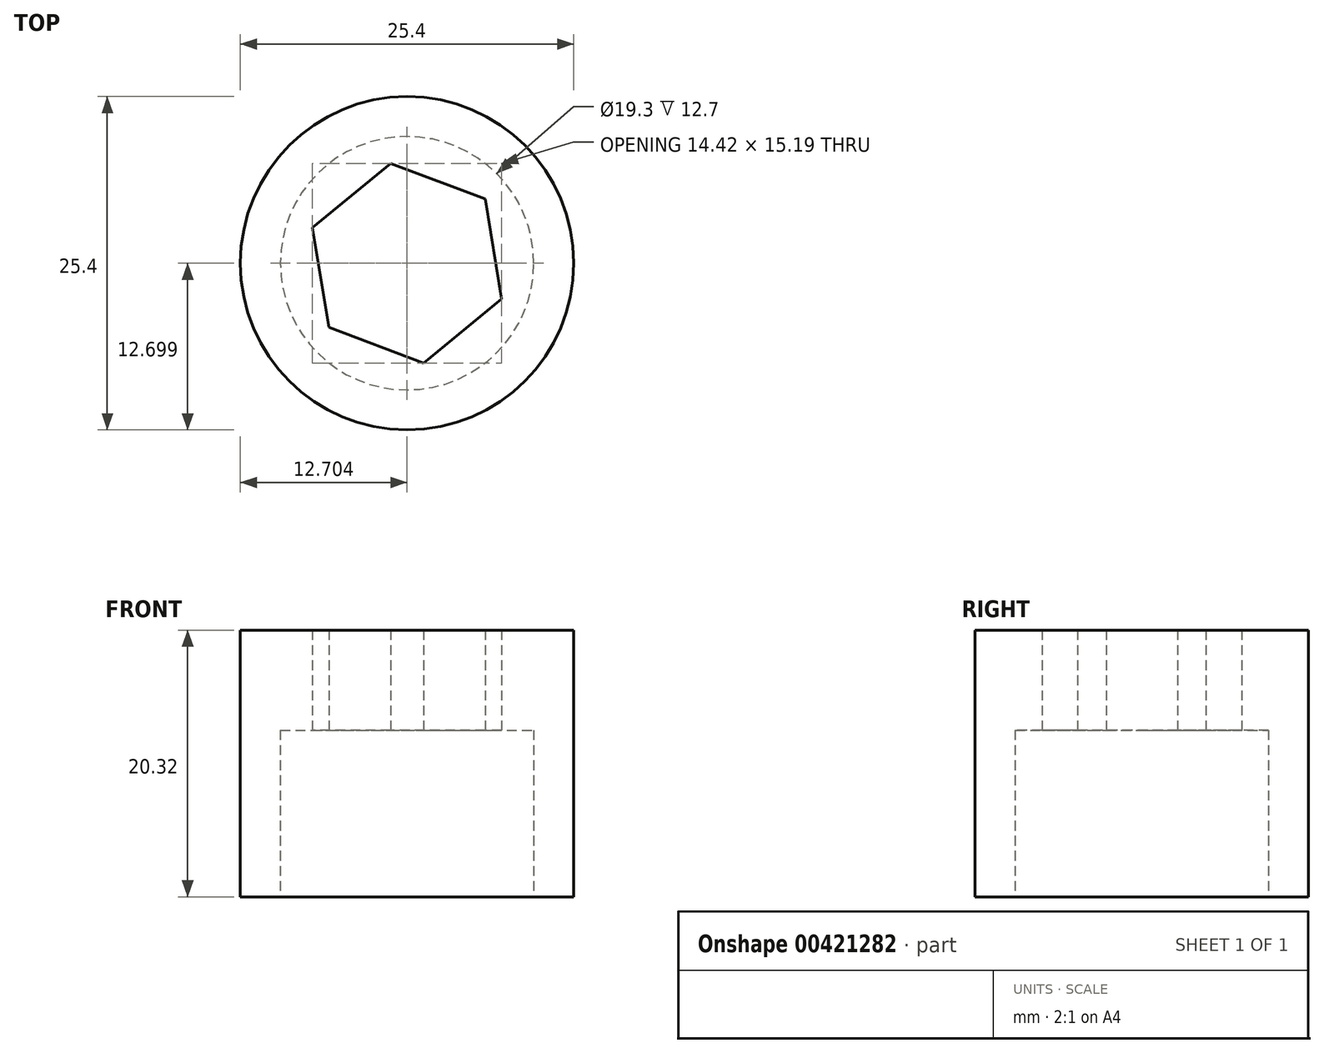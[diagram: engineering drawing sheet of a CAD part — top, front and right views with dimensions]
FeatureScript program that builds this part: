
annotation { "Feature Type Name" : "Feature", "Feature Type Description" : "" }
export const myFeature = defineFeature(function(context is Context, id is Id, definition is map)
    precondition{}
    {
        {
            var Q0;
            Q0=qCreatedBy(makeId("Top.planeOp"),FACE);
            var sketch = newSketch(context, id + "F0", { "sketchPlane" : qUnion([Q0])});
            skCircle(sketch, "E0", {"center": v(-39.24, 31.02) * mm, "radius": 12.7 * mm});
            skCircle(sketch, "E1", {"center": v(-39.24, 31.02) * mm, "radius": 10.16 * mm});
            skCircle(sketch, "E2.cCircle", {"center": v(-39.24, 31.02) * mm, "radius": 7.7 * mm, "construction": true});
            skLineSegment(sketch, "E2.0", {"start": v(-33.29, 35.9) * mm, "end": v(-32.03, 28.31) * mm});
            skLineSegment(sketch, "E2.1", {"start": v(-32.03, 28.31) * mm, "end": v(-37.97, 23.42) * mm});
            skLineSegment(sketch, "E2.2", {"start": v(-37.97, 23.42) * mm, "end": v(-45.18, 26.13) * mm});
            skLineSegment(sketch, "E2.3", {"start": v(-45.18, 26.13) * mm, "end": v(-46.44, 33.72) * mm});
            skLineSegment(sketch, "E2.4", {"start": v(-46.44, 33.72) * mm, "end": v(-40.5, 38.61) * mm});
            skLineSegment(sketch, "E2.5", {"start": v(-40.5, 38.61) * mm, "end": v(-33.29, 35.9) * mm});
            skSolve(sketch);
        }
        {
            var Q0;
            Q0=makeQuery(id+"F0.imprint","IMPRINT",FACE,{"disambiguationData":[TD([[makeQuery(id+"F0.imprint","IMPRINT",EDGE,{"derivedFrom":sQuery(id+"F0.wireOp",EDGE,"E0")}),1.0]])]});
            extrude(context, id + "F1", {"entities" : qUnion([Q0]), "depth" : 20.32 * mm, "offsetDistance" : 25.4 * mm});
        }
        {
            var Q0;
            Q0=makeQuery(id+"F0.imprint","IMPRINT",FACE,{"disambiguationData":[TD([[makeQuery(id+"F0.imprint","IMPRINT",EDGE,{"derivedFrom":sQuery(id+"F0.wireOp",EDGE,"E1")}),1.0]])]});
            extrude(context, id + "F2", {"entities" : qUnion([Q0]), "operationType" : NewBodyOperationType.ADD, "depth" : 20.32 * mm, "offsetDistance" : 25.4 * mm});
        }
        {
            var Q0;
            {var subQ0=sQuery(id+"F0.wireOp",EDGE,"E1");Q0=makeQuery(id+"F2.boolean.opBoolean","MERGE",FACE,{"derivedFrom":[makeQuery(id+"F1.opExtrude","CAP_FACE",FACE,{"disambiguationData":[OSD([sQuery(id+"F0.wireOp",EDGE,"E0"),subQ0])],"isStart":true}),makeQuery(id+"F2.opExtrude","CAP_FACE",FACE,{"disambiguationData":[OSD([subQ0,sQuery(id+"F0.wireOp",EDGE,"E2.0"),sQuery(id+"F0.wireOp",EDGE,"E2.1"),sQuery(id+"F0.wireOp",EDGE,"E2.2"),sQuery(id+"F0.wireOp",EDGE,"E2.3"),sQuery(id+"F0.wireOp",EDGE,"E2.4"),sQuery(id+"F0.wireOp",EDGE,"E2.5")])],"isStart":true})]});}
            var sketch = newSketch(context, id + "F3", { "sketchPlane" : qUnion([Q0])});
            skCircle(sketch, "E3", {"center": v(-39.24, -31.02) * mm, "radius": 9.65 * mm});
            skSolve(sketch);
        }
        {
            var Q0;
            Q0 = qSketchRegion(id + "F3", true);
            extrude(context, id + "F4", {"entities" : qUnion([Q0]), "operationType" : NewBodyOperationType.REMOVE, "oppositeDirection" : true, "depth" : 12.7 * mm, "offsetDistance" : 25.4 * mm});
        }
    });
